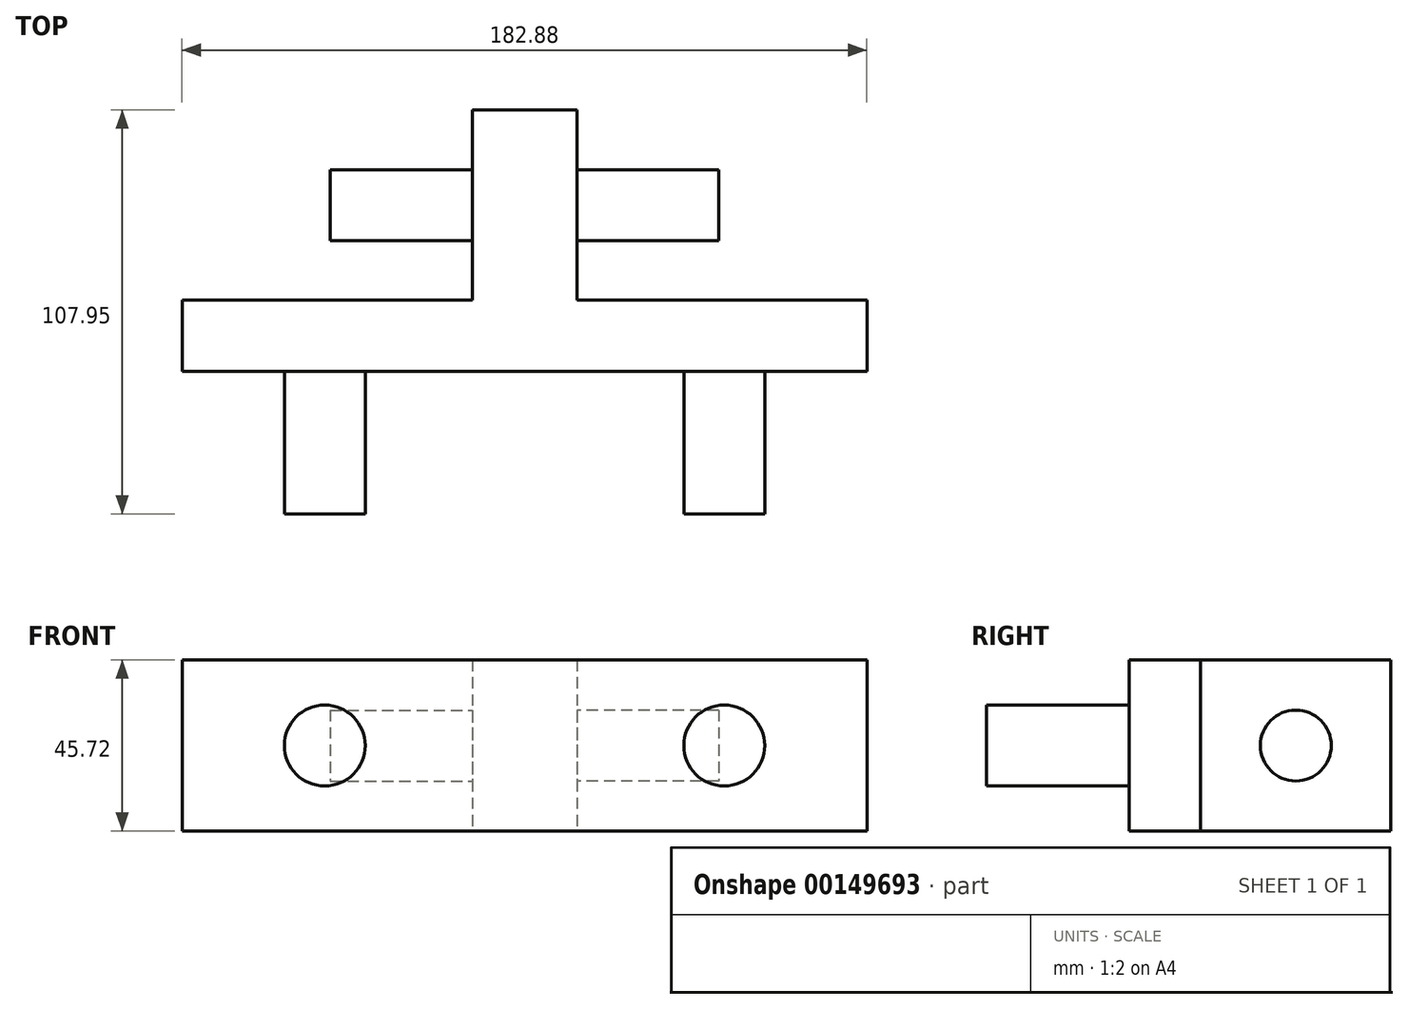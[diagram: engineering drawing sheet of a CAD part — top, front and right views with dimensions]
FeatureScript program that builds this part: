
annotation { "Feature Type Name" : "Feature", "Feature Type Description" : "" }
export const myFeature = defineFeature(function(context is Context, id is Id, definition is map)
    precondition{}
    {
        {
            var Q0;
            Q0=qCreatedBy(makeId("Front.planeOp"),FACE);
            var sketch = newSketch(context, id + "F0", { "sketchPlane" : qUnion([Q0])});
            skLineSegment(sketch, "E0.bottom", {"start": v(-74.7, 40.91) * mm, "end": v(108.18, 40.91) * mm});
            skLineSegment(sketch, "E0.top", {"start": v(-74.7, -4.8) * mm, "end": v(108.18, -4.8) * mm});
            skLineSegment(sketch, "E0.left", {"start": v(-74.7, 40.91) * mm, "end": v(-74.7, -4.8) * mm});
            skLineSegment(sketch, "E0.right", {"start": v(108.18, 40.91) * mm, "end": v(108.18, -4.8) * mm});
            skLineSegment(sketch, "E1", {"start": v(108.18, 40.91) * mm, "end": v(42.14, 40.91) * mm});
            skLineSegment(sketch, "E2", {"start": v(-74.7, 40.91) * mm, "end": v(-8.66, 40.91) * mm});
            skLineSegment(sketch, "E3", {"start": v(42.14, 40.91) * mm, "end": v(30.71, 40.91) * mm});
            skLineSegment(sketch, "E4", {"start": v(-8.66, 40.91) * mm, "end": v(2.77, 40.91) * mm});
            skLineSegment(sketch, "E5.bottom", {"start": v(30.71, 40.91) * mm, "end": v(2.77, 40.91) * mm});
            skLineSegment(sketch, "E5.top", {"start": v(30.71, -4.8) * mm, "end": v(2.77, -4.8) * mm});
            skLineSegment(sketch, "E5.left", {"start": v(30.71, 40.91) * mm, "end": v(30.71, -4.8) * mm});
            skLineSegment(sketch, "E5.right", {"start": v(2.77, 40.91) * mm, "end": v(2.77, -4.8) * mm});
            skSolve(sketch);
        }
        {
            var Q0;
            Q0 = qSketchRegion(id + "F0", true);
            extrude(context, id + "F1", {"entities" : qUnion([Q0]), "depth" : 19.05 * mm});
        }
        {
            var Q0;
            Q0=makeQuery(id+"F1.opExtrude","CAP_FACE",FACE,{"disambiguationData":[OSD([sQuery(id+"F0.wireOp",EDGE,"E0.bottom"),sQuery(id+"F0.wireOp",EDGE,"E0.top"),sQuery(id+"F0.wireOp",EDGE,"E0.left"),sQuery(id+"F0.wireOp",EDGE,"E0.right")])],"isStart":true});
            var sketch = newSketch(context, id + "F2", { "sketchPlane" : qUnion([Q0])});
            skLineSegment(sketch, "E6", {"start": v(-108.18, 40.91) * mm, "end": v(-30.71, 40.91) * mm});
            skLineSegment(sketch, "E7", {"start": v(74.7, 40.91) * mm, "end": v(-2.77, 40.91) * mm});
            skLineSegment(sketch, "E8.bottom", {"start": v(-30.71, 40.91) * mm, "end": v(-2.77, 40.91) * mm});
            skLineSegment(sketch, "E8.top", {"start": v(-30.71, -4.8) * mm, "end": v(-2.77, -4.8) * mm});
            skLineSegment(sketch, "E8.left", {"start": v(-30.71, 40.91) * mm, "end": v(-30.71, -4.8) * mm});
            skLineSegment(sketch, "E8.right", {"start": v(-2.77, 40.91) * mm, "end": v(-2.77, -4.8) * mm});
            skSolve(sketch);
        }
        {
            var Q0;
            Q0 = qSketchRegion(id + "F2", true);
            extrude(context, id + "F3", {"entities" : qUnion([Q0]), "operationType" : NewBodyOperationType.ADD, "depth" : 50.8 * mm});
        }
        {
            var Q0;
            Q0=makeQuery(id+"F3.opExtrude","SWEPT_FACE",FACE,{"disambiguationData":[OSD([sQuery(id+"F2.wireOp",EDGE,"E8.right")])]});
            var sketch = newSketch(context, id + "F4", { "sketchPlane" : qUnion([Q0])});
            skLineSegment(sketch, "E9", {"start": v(-50.8, 18.05) * mm, "end": v(-25.4, 18.05) * mm});
            skCircle(sketch, "E10", {"center": v(-25.4, 18.05) * mm, "radius": 9.46 * mm});
            skSolve(sketch);
        }
        {
            var Q0;
            Q0=makeQuery(id+"F3.opExtrude","SWEPT_FACE",FACE,{"disambiguationData":[OSD([sQuery(id+"F2.wireOp",EDGE,"E8.left")])]});
            var sketch = newSketch(context, id + "F5", { "sketchPlane" : qUnion([Q0])});
            skLineSegment(sketch, "E11", {"start": v(50.8, 18.05) * mm, "end": v(25.4, 18.05) * mm});
            skCircle(sketch, "E12", {"center": v(25.4, 18.05) * mm, "radius": 9.46 * mm});
            skSolve(sketch);
        }
        {
            var Q0;
            Q0 = qSketchRegion(id + "F5", true);
            extrude(context, id + "F6", {"entities" : qUnion([Q0]), "operationType" : NewBodyOperationType.ADD, "depth" : 37.85 * mm});
        }
        {
            var Q0;
            Q0 = qSketchRegion(id + "F4", true);
            extrude(context, id + "F7", {"entities" : qUnion([Q0]), "operationType" : NewBodyOperationType.ADD, "depth" : 37.85 * mm});
        }
        {
            var Q0;
            Q0=makeQuery(id+"F1.opExtrude","CAP_FACE",FACE,{"disambiguationData":[OSD([sQuery(id+"F0.wireOp",EDGE,"E0.top"),sQuery(id+"F0.wireOp",EDGE,"E0.left"),sQuery(id+"F0.wireOp",EDGE,"E0.right"),sQuery(id+"F0.wireOp",EDGE,"E1"),sQuery(id+"F0.wireOp",EDGE,"E2"),sQuery(id+"F0.wireOp",EDGE,"E3"),sQuery(id+"F0.wireOp",EDGE,"E4"),sQuery(id+"F0.wireOp",EDGE,"E5.bottom"),sQuery(id+"F0.wireOp",EDGE,"E5.top")])],"isStart":false});
            var sketch = newSketch(context, id + "F8", { "sketchPlane" : qUnion([Q0])});
            skLineSegment(sketch, "E13", {"start": v(-74.7, 18.05) * mm, "end": v(108.18, 18.05) * mm});
            skLineSegment(sketch, "E14", {"start": v(-74.7, 18.05) * mm, "end": v(-36.6, 18.05) * mm});
            skLineSegment(sketch, "E15", {"start": v(108.18, 18.05) * mm, "end": v(70.08, 18.05) * mm});
            skCircle(sketch, "E16", {"center": v(-36.6, 18.05) * mm, "radius": 10.8 * mm});
            skCircle(sketch, "E17", {"center": v(70.08, 18.05) * mm, "radius": 10.8 * mm});
            skSolve(sketch);
        }
        {
            var Q0;
            Q0 = qSketchRegion(id + "F8", true);
            extrude(context, id + "F9", {"entities" : qUnion([Q0]), "operationType" : NewBodyOperationType.ADD, "depth" : 38.1 * mm});
        }
    });
